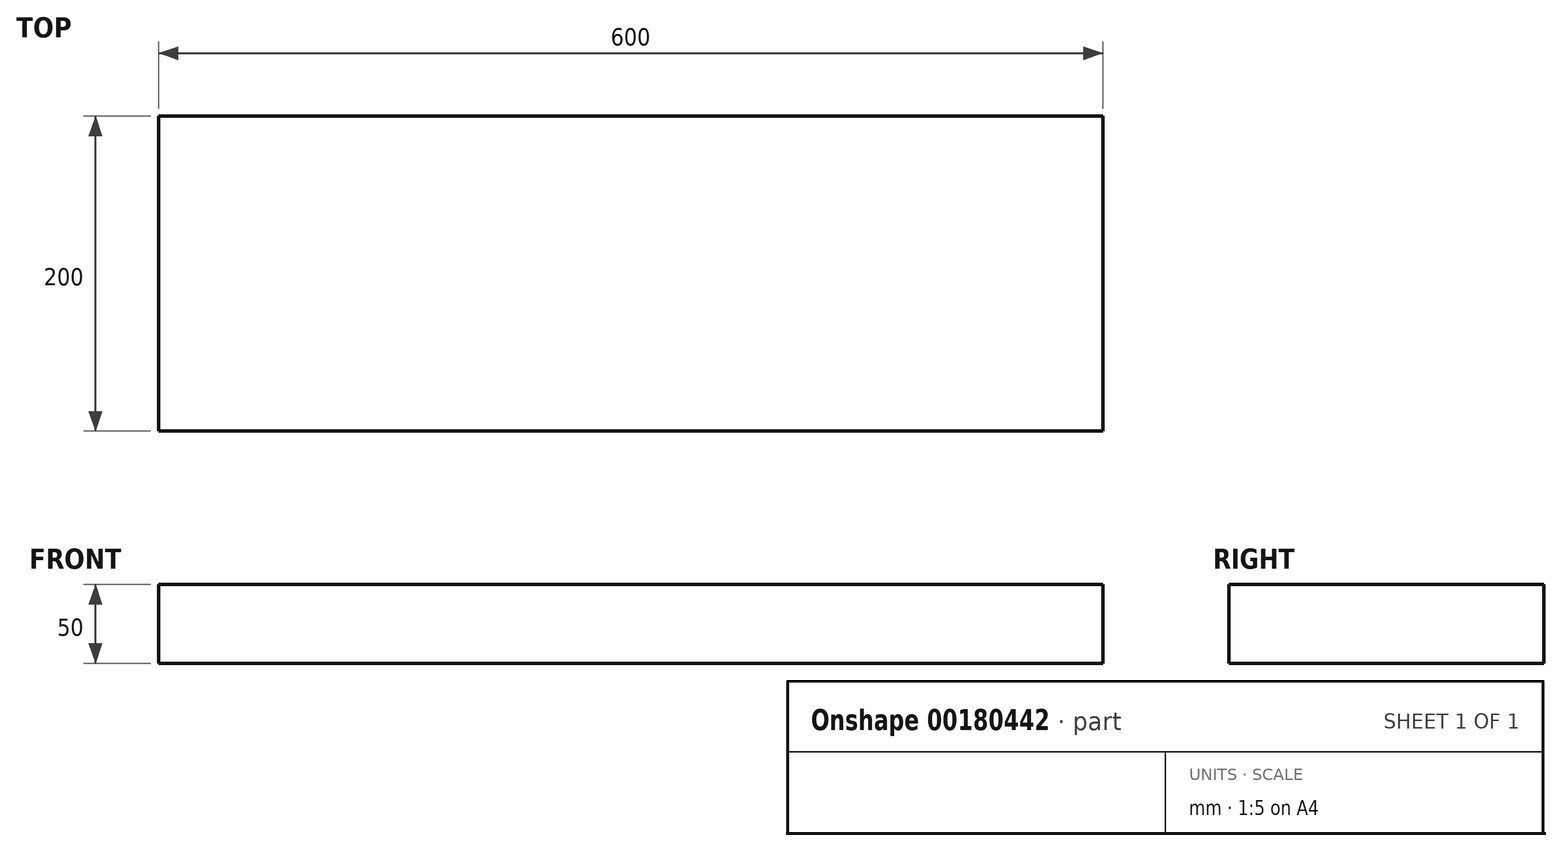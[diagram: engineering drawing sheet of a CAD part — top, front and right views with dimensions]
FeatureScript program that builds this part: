
annotation { "Feature Type Name" : "Feature", "Feature Type Description" : "" }
export const myFeature = defineFeature(function(context is Context, id is Id, definition is map)
    precondition{}
    {
        {
            var Q0;
            Q0=qCreatedBy(makeId("Top.planeOp"),FACE);
            var sketch = newSketch(context, id + "F0", { "sketchPlane" : qUnion([Q0])});
            skLineSegment(sketch, "E0.bottom", {"start": v(300, -100) * mm, "end": v(-300, -100) * mm});
            skLineSegment(sketch, "E0.top", {"start": v(300, 100) * mm, "end": v(-300, 100) * mm});
            skLineSegment(sketch, "E0.left", {"start": v(300, -100) * mm, "end": v(300, 100) * mm});
            skLineSegment(sketch, "E0.right", {"start": v(-300, -100) * mm, "end": v(-300, 100) * mm});
            skPoint(sketch, "E0.middle", {"position": v(0, 0) * mm});
            skSolve(sketch);
        }
        {
            var Q0;
            Q0 = qSketchRegion(id + "F0", true);
            extrude(context, id + "F1", {"entities" : qUnion([Q0]), "depth" : 50 * mm});
        }
        {
            var Q0;
            Q0=qCreatedBy(makeId("Top.planeOp"),FACE);
            cPlane(context, id + "F2", {"entities" : qUnion([Q0]), "cplaneType" : CPlaneType.OFFSET, "offset" : 25 * mm, "width" : 150 * mm, "height" : 150 * mm});
        }
        {
            var Q0;
            Q0=qCreatedBy(makeId("Top.planeOp"),FACE);
            cPlane(context, id + "F3", {"entities" : qUnion([Q0]), "cplaneType" : CPlaneType.OFFSET, "offset" : 75 * mm, "width" : 150 * mm, "height" : 150 * mm});
        }
    });
